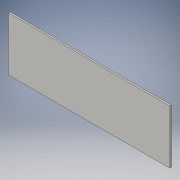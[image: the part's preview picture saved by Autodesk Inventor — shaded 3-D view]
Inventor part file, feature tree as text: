
AUTODESK INVENTOR PART (.ipt)
format: ipt  version: 2016 (Build 200138000, 138)  size: 83,456 bytes
history: native  units: in
note: dims shown in document units (in); Inventor stores cm internally (conversion verified against a paired STEP export)
features: extrude x1, sketch x1
ambient origin geometry x8: Origin, YZ Plane, XZ Plane, XY Plane, X Axis, Y Axis, Z Axis, Center Point
bodies: Solid1 (feature_tree)
feature tree (2):
  extrude  "Extrusion1"  Depth=3.0in
  sketch  "Sketch1"  dims[d0=9.0in d1=3.0in d2=0.1in d3=0.0in]
